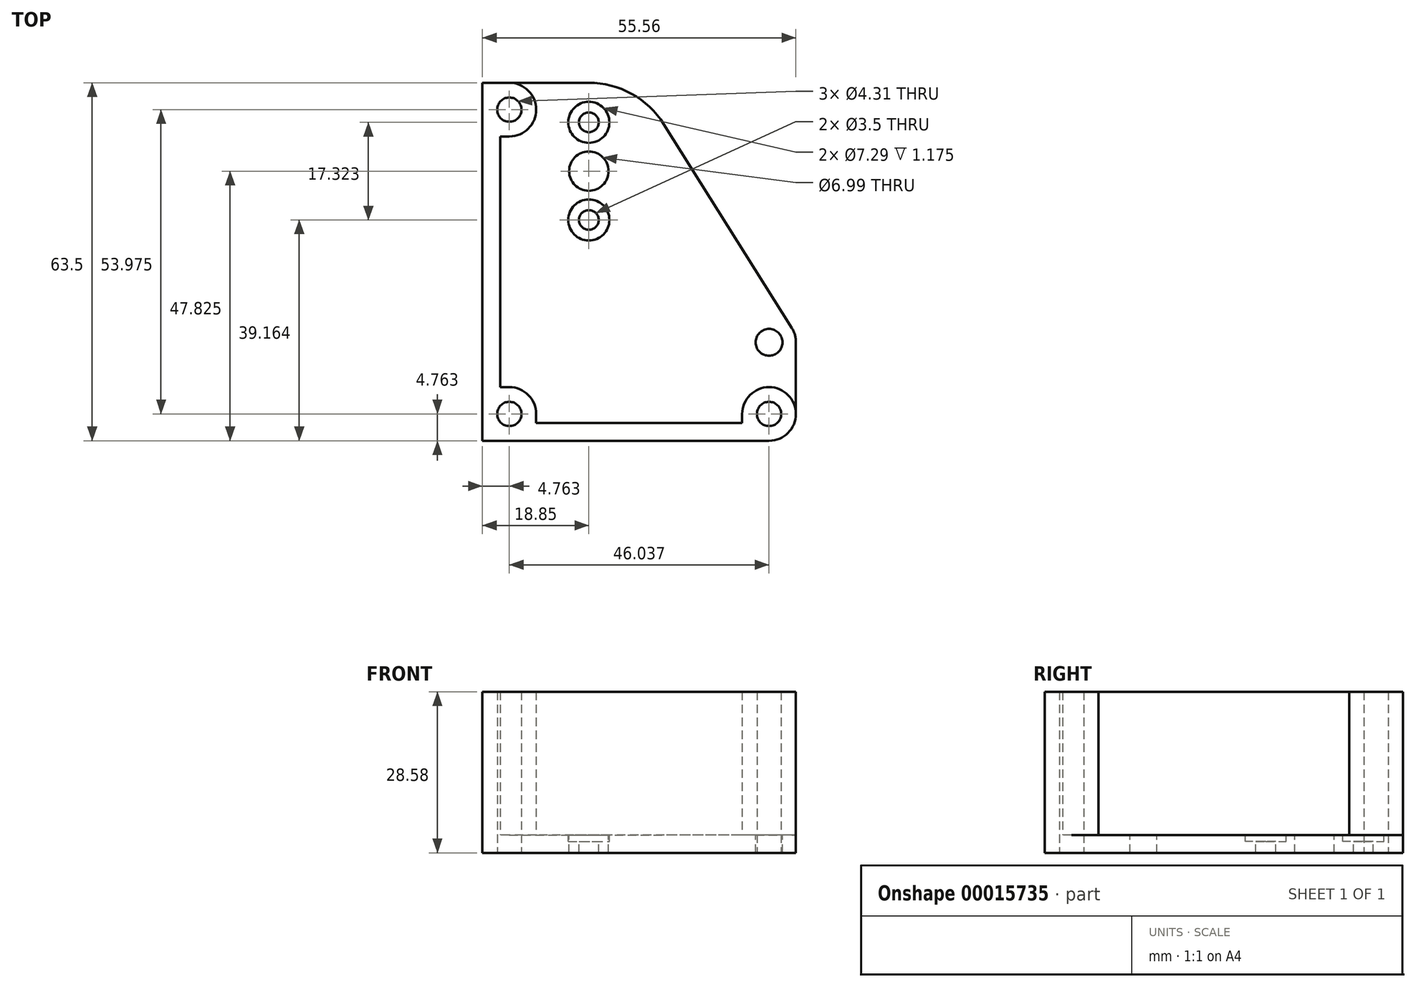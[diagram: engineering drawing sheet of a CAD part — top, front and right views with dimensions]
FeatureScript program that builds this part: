
annotation { "Feature Type Name" : "Feature", "Feature Type Description" : "" }
export const myFeature = defineFeature(function(context is Context, id is Id, definition is map)
    precondition{}
    {
        {
            var Q0;
            Q0=qCreatedBy(makeId("Top.planeOp"),FACE);
            var sketch = newSketch(context, id + "F0", { "sketchPlane" : qUnion([Q0])});
            skLineSegment(sketch, "E0.bottom", {"start": v(0, 0) * mm, "end": v(50.8, 0) * mm});
            skLineSegment(sketch, "E0.left", {"start": v(0, 0) * mm, "end": v(0, 63.5) * mm});
            skLineSegment(sketch, "E1", {"start": v(4.76, 0) * mm, "end": v(4.76, 4.76) * mm, "construction": true});
            skLineSegment(sketch, "E2", {"start": v(4.76, 4.76) * mm, "end": v(0, 4.76) * mm, "construction": true});
            skCircle(sketch, "E3", {"center": v(4.76, 4.76) * mm, "radius": 2.15 * mm});
            skCircle(sketch, "E4", {"center": v(50.8, 4.76) * mm, "radius": 2.15 * mm});
            skArc(sketch, "E5", {"start": v(50.8, 0) * mm, "mid": v(54.17, 8.13) * mm, "end": v(46.04, 4.76) * mm});
            skLineSegment(sketch, "E6", {"start": v(46.04, 4.76) * mm, "end": v(46.04, 3.18) * mm});
            skLineSegment(sketch, "E7", {"start": v(46.04, 3.18) * mm, "end": v(9.53, 3.17) * mm});
            skLineSegment(sketch, "E8", {"start": v(9.53, 4.76) * mm, "end": v(9.53, 3.17) * mm});
            skArc(sketch, "E9", {"start": v(9.53, 4.76) * mm, "mid": v(8.13, 8.13) * mm, "end": v(4.76, 9.52) * mm});
            skLineSegment(sketch, "E10", {"start": v(46.04, 3.18) * mm, "end": v(46.04, 0) * mm, "construction": true});
            skLineSegment(sketch, "E11", {"start": v(4.76, 9.52) * mm, "end": v(3.18, 9.52) * mm});
            skLineSegment(sketch, "E12", {"start": v(3.18, 9.52) * mm, "end": v(3.18, 53.98) * mm});
            skLineSegment(sketch, "E13", {"start": v(0, 63.5) * mm, "end": v(4.76, 63.5) * mm});
            skArc(sketch, "E14", {"start": v(4.76, 53.97) * mm, "mid": v(9.52, 58.74) * mm, "end": v(4.76, 63.5) * mm});
            skLineSegment(sketch, "E15", {"start": v(3.17, 53.98) * mm, "end": v(4.76, 53.98) * mm});
            skCircle(sketch, "E16", {"center": v(4.76, 58.74) * mm, "radius": 2.15 * mm});
            skSolve(sketch);
        }
        {
            var Q0;
            Q0=qSketchRegion(id+"F0",true);
            extrude(context, id + "F1", {"entities" : qUnion([Q0]), "depth" : 25.4 * mm});
        }
        {
            var Q0;
            Q0=makeQuery(id+"F1.opExtrude","CAP_FACE",FACE,{"disambiguationData":[OSD([sQuery(id+"F0.wireOp",EDGE,"E0.bottom"),sQuery(id+"F0.wireOp",EDGE,"E0.left"),sQuery(id+"F0.wireOp",EDGE,"E3"),sQuery(id+"F0.wireOp",EDGE,"E4"),sQuery(id+"F0.wireOp",EDGE,"E5"),sQuery(id+"F0.wireOp",EDGE,"E6"),sQuery(id+"F0.wireOp",EDGE,"E7"),sQuery(id+"F0.wireOp",EDGE,"E8"),sQuery(id+"F0.wireOp",EDGE,"E9"),sQuery(id+"F0.wireOp",EDGE,"E11"),sQuery(id+"F0.wireOp",EDGE,"E12"),sQuery(id+"F0.wireOp",EDGE,"E13"),sQuery(id+"F0.wireOp",EDGE,"E14"),sQuery(id+"F0.wireOp",EDGE,"E15"),sQuery(id+"F0.wireOp",EDGE,"E16")])],"isStart":true});
            var sketch = newSketch(context, id + "F2", { "sketchPlane" : qUnion([Q0])});
            skLineSegment(sketch, "E17", {"start": v(55.56, -17.46) * mm, "end": v(55.56, -4.76) * mm});
            skLineSegment(sketch, "E18.bottom", {"start": v(50.8, 0) * mm, "end": v(0, 0) * mm});
            skLineSegment(sketch, "E18.right", {"start": v(0, -63.5) * mm, "end": v(0, 0) * mm});
            skCircle(sketch, "E19", {"center": v(18.85, -47.82) * mm, "radius": 12.5 * mm, "construction": true});
            skLineSegment(sketch, "E20", {"start": v(18.85, -47.82) * mm, "end": v(6.35, -47.82) * mm, "construction": true});
            skLineSegment(sketch, "E21", {"start": v(6.35, -47.82) * mm, "end": v(3.18, -47.82) * mm, "construction": true});
            skLineSegment(sketch, "E22", {"start": v(50.8, -17.46) * mm, "end": v(50.8, -4.76) * mm, "construction": true});
            skCircle(sketch, "E23", {"center": v(4.76, -58.74) * mm, "radius": 2.15 * mm});
            skCircle(sketch, "E24", {"center": v(50.8, -4.76) * mm, "radius": 2.15 * mm});
            skCircle(sketch, "E25", {"center": v(4.76, -4.76) * mm, "radius": 2.15 * mm});
            skCircle(sketch, "E26", {"center": v(50.8, -17.46) * mm, "radius": 2.38 * mm});
            skLineSegment(sketch, "E27", {"start": v(18.85, -39.16) * mm, "end": v(18.85, -56.49) * mm, "construction": true});
            skCircle(sketch, "E28", {"center": v(18.85, -47.82) * mm, "radius": 3.5 * mm});
            skCircle(sketch, "E29", {"center": v(18.85, -39.16) * mm, "radius": 1.75 * mm});
            skCircle(sketch, "E30", {"center": v(18.85, -56.49) * mm, "radius": 1.75 * mm});
            skArc(sketch, "E31", {"start": v(18.85, -63.5) * mm, "mid": v(26.43, -61.54) * mm, "end": v(32.13, -56.16) * mm});
            skArc(sketch, "E32", {"start": v(54.83, -20) * mm, "mid": v(55.38, -18.78) * mm, "end": v(55.56, -17.46) * mm});
            skLineSegment(sketch, "E33", {"start": v(0, -63.5) * mm, "end": v(18.85, -63.5) * mm});
            skLineSegment(sketch, "E34", {"start": v(54.83, -20) * mm, "end": v(32.13, -56.16) * mm});
            skSolve(sketch);
        }
        {
            var Q0;
            {var subQ1=sQuery(id+"F2.wireOp",EDGE,"E17");Q0=makeQuery(id+"F2.imprint","IMPRINT",FACE,{"disambiguationData":[TD([[makeQuery(id+"F2.imprint","IMPRINT",EDGE,{"derivedFrom":subQ1}),1.0]])]});}
            var Q1;
            {var subQ0=sQuery(id+"F2.wireOp",EDGE,"E18.bottom");Q1=makeQuery(id+"F2.imprint","IMPRINT",FACE,{"disambiguationData":[TD([[makeQuery(id+"F2.imprint","IMPRINT",EDGE,{"derivedFrom":subQ0}),1.0]])]});}
            var Q2;
            {var subQ4=sQuery(id+"F2.wireOp",EDGE,"E18.bottom");Q2=makeQuery(id+"F2.imprint","IMPRINT",FACE,{"disambiguationData":[TD([[makeQuery(id+"F2.imprint","IMPRINT",EDGE,{"derivedFrom":subQ4}),-1.0]])]});}
            extrude(context, id + "F3", {"entities" : qUnion([Q0, Q1, Q2]), "operationType" : NewBodyOperationType.ADD, "depth" : 3.17 * mm});
        }
        {
            var Q0;
            Q0=makeQuery(id+"F3.opExtrude","CAP_FACE",FACE,{"disambiguationData":[OSD([sQuery(id+"F0.wireOp",EDGE,"E5"),sQuery(id+"F2.wireOp",EDGE,"E17"),sQuery(id+"F2.wireOp",EDGE,"E18.bottom"),sQuery(id+"F2.wireOp",EDGE,"E18.right"),sQuery(id+"F2.wireOp",EDGE,"E23"),sQuery(id+"F2.wireOp",EDGE,"E24"),sQuery(id+"F2.wireOp",EDGE,"E25"),sQuery(id+"F2.wireOp",EDGE,"E26"),sQuery(id+"F2.wireOp",EDGE,"E28"),sQuery(id+"F2.wireOp",EDGE,"E29"),sQuery(id+"F2.wireOp",EDGE,"E30"),sQuery(id+"F2.wireOp",EDGE,"E31"),sQuery(id+"F2.wireOp",EDGE,"E32"),sQuery(id+"F2.wireOp",EDGE,"E33"),sQuery(id+"F2.wireOp",EDGE,"E34")])],"isStart":false});
            cPlane(context, id + "F4", {"entities" : qUnion([Q0]), "cplaneType" : CPlaneType.OFFSET, "offset" : 2 * mm, "oppositeDirection" : true, "width" : 152.4 * mm, "height" : 152.4 * mm});
        }
        {
            var Q0;
            Q0=makeQuery(id+"F3.opExtrude","CAP_FACE",FACE,{"disambiguationData":[OSD([sQuery(id+"F0.wireOp",EDGE,"E5"),sQuery(id+"F2.wireOp",EDGE,"E17"),sQuery(id+"F2.wireOp",EDGE,"E18.bottom"),sQuery(id+"F2.wireOp",EDGE,"E18.right"),sQuery(id+"F2.wireOp",EDGE,"E23"),sQuery(id+"F2.wireOp",EDGE,"E24"),sQuery(id+"F2.wireOp",EDGE,"E25"),sQuery(id+"F2.wireOp",EDGE,"E26"),sQuery(id+"F2.wireOp",EDGE,"E28"),sQuery(id+"F2.wireOp",EDGE,"E29"),sQuery(id+"F2.wireOp",EDGE,"E30"),sQuery(id+"F2.wireOp",EDGE,"E31"),sQuery(id+"F2.wireOp",EDGE,"E32"),sQuery(id+"F2.wireOp",EDGE,"E33"),sQuery(id+"F2.wireOp",EDGE,"E34")])],"isStart":true});
            var sketch = newSketch(context, id + "F5", { "sketchPlane" : qUnion([Q0])});
            skCircle(sketch, "E35", {"center": v(18.85, 39.16) * mm, "radius": 3.64 * mm});
            skCircle(sketch, "E36", {"center": v(18.85, 56.49) * mm, "radius": 3.64 * mm});
            skSolve(sketch);
        }
        {
            var Q0;
            Q0 = qSketchRegion(id + "F5", true);
            var Q1;
            Q1=qCreatedBy(id+"F4.planeOp",FACE);
            extrude(context, id + "F6", {"entities" : qUnion([Q0]), "operationType" : NewBodyOperationType.REMOVE, "endBound" : BoundingType.UP_TO_SURFACE, "oppositeDirection" : true, "endBoundEntityFace" : qUnion([Q1]), "depth" : 25.4 * mm});
        }
    });
